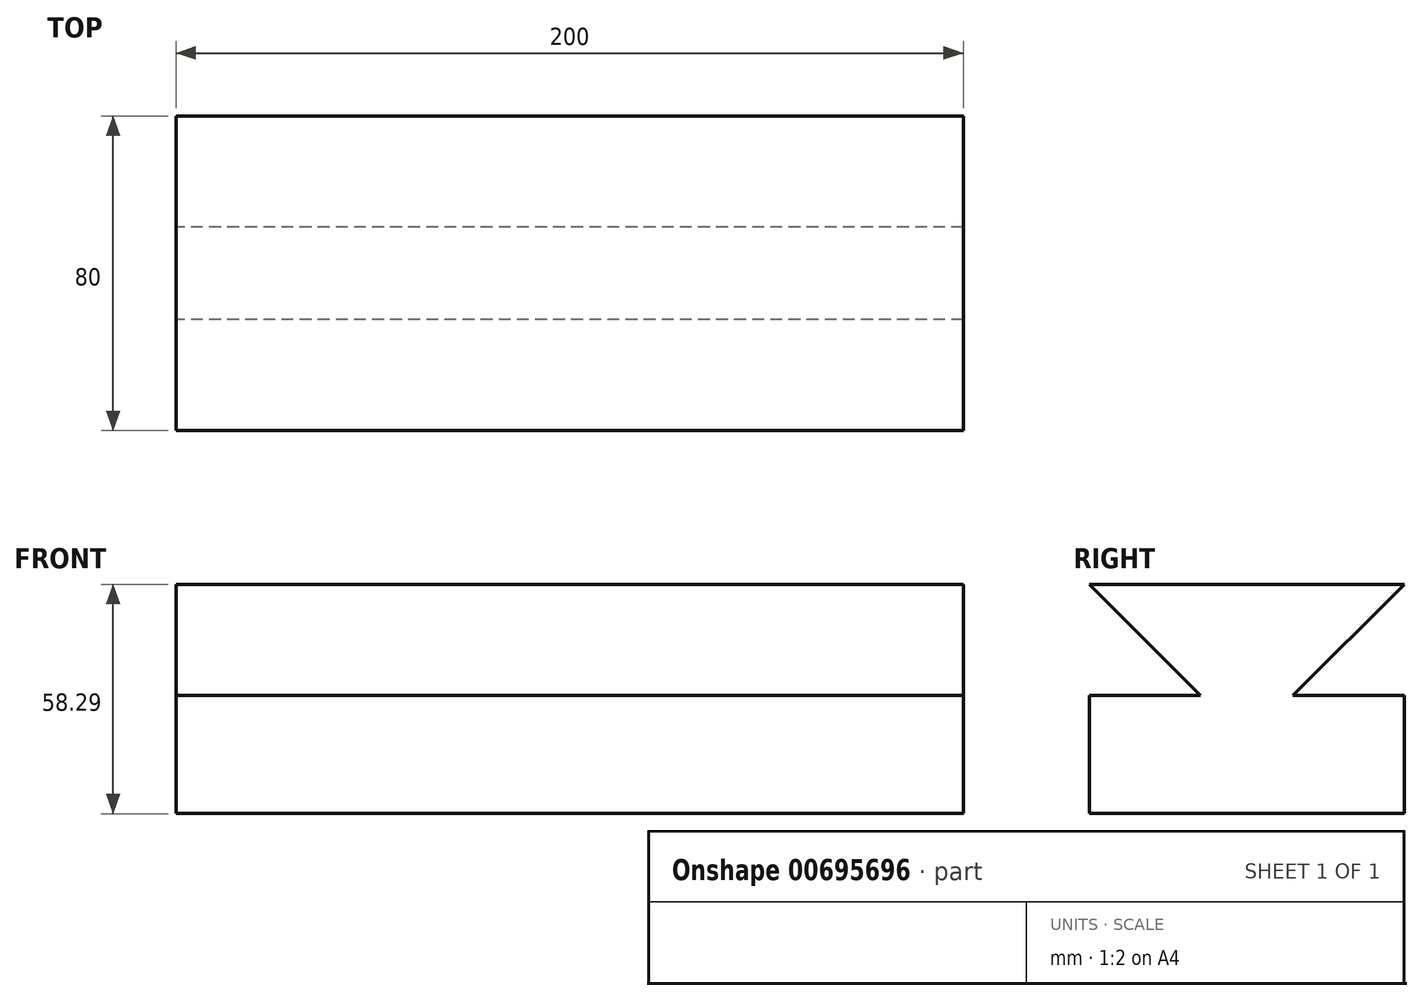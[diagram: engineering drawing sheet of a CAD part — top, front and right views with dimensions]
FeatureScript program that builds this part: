
annotation { "Feature Type Name" : "Feature", "Feature Type Description" : "" }
export const myFeature = defineFeature(function(context is Context, id is Id, definition is map)
    precondition{}
    {
        {
            var Q0;
            Q0=qCreatedBy(makeId("Right.planeOp"),FACE);
            var sketch = newSketch(context, id + "F0", { "sketchPlane" : qUnion([Q0])});
            skLineSegment(sketch, "E0", {"start": v(-40.72, 39) * mm, "end": v(39.28, 39) * mm});
            skLineSegment(sketch, "E1", {"start": v(-40.72, 39) * mm, "end": v(-12.44, 10.71) * mm});
            skLineSegment(sketch, "E2", {"start": v(-40.72, 10.71) * mm, "end": v(39.28, 10.71) * mm});
            skLineSegment(sketch, "E3", {"start": v(39.28, 39) * mm, "end": v(11, 10.71) * mm});
            skLineSegment(sketch, "E4", {"start": v(-40.72, 10.71) * mm, "end": v(-40.72, -19.29) * mm});
            skLineSegment(sketch, "E5", {"start": v(39.28, 10.71) * mm, "end": v(39.28, -19.29) * mm});
            skLineSegment(sketch, "E6", {"start": v(39.28, -19.29) * mm, "end": v(-40.72, -19.29) * mm});
            skSolve(sketch);
        }
        {
            var Q0;
            Q0 = qSketchRegion(id + "F0", true);
            extrude(context, id + "F1", {"entities" : qUnion([Q0]), "depth" : 200 * mm, "offsetDistance" : 25 * mm});
        }
    });
